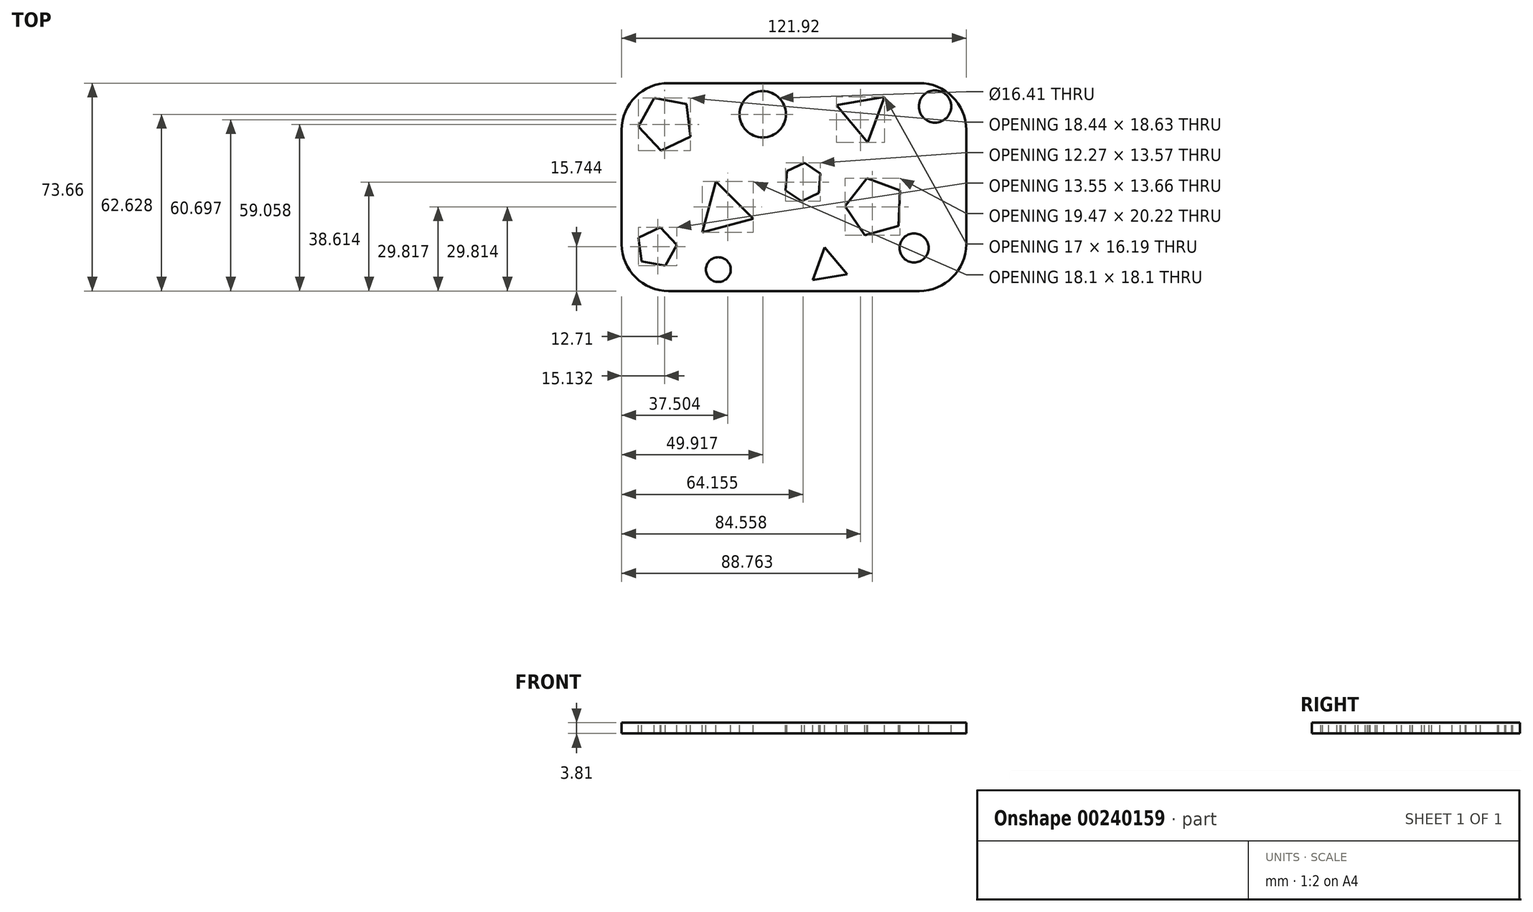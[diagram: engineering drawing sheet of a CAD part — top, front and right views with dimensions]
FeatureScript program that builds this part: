
annotation { "Feature Type Name" : "Feature", "Feature Type Description" : "" }
export const myFeature = defineFeature(function(context is Context, id is Id, definition is map)
    precondition{}
    {
        {
            var Q0;
            Q0=qCreatedBy(makeId("Top.planeOp"),FACE);
            var sketch = newSketch(context, id + "F0", { "sketchPlane" : qUnion([Q0])});
            skLineSegment(sketch, "E0.bottom", {"start": v(-58.63, 50.24) * mm, "end": v(63.29, 50.24) * mm});
            skLineSegment(sketch, "E0.top", {"start": v(-58.63, -23.42) * mm, "end": v(63.29, -23.42) * mm});
            skLineSegment(sketch, "E0.left", {"start": v(-58.63, 50.24) * mm, "end": v(-58.63, -23.42) * mm});
            skLineSegment(sketch, "E0.right", {"start": v(63.29, 50.24) * mm, "end": v(63.29, -23.42) * mm});
            skSolve(sketch);
        }
        {
            var Q0;
            Q0 = qSketchRegion(id + "F0", true);
            extrude(context, id + "F1", {"entities" : qUnion([Q0]), "depth" : 3.8 * mm});
        }
        {
            var Q0;
            Q0=makeQuery(id+"F1.opExtrude","SWEPT_EDGE",EDGE,{"disambiguationData":[OSD([sQuery(id+"F0.wireOp",EDGE,"E0.top"),sQuery(id+"F0.wireOp",EDGE,"E0.left")])]});
            var Q1;
            Q1=makeQuery(id+"F1.opExtrude","SWEPT_EDGE",EDGE,{"disambiguationData":[OSD([sQuery(id+"F0.wireOp",EDGE,"E0.top"),sQuery(id+"F0.wireOp",EDGE,"E0.right")])]});
            var Q2;
            Q2=makeQuery(id+"F1.opExtrude","SWEPT_EDGE",EDGE,{"disambiguationData":[OSD([sQuery(id+"F0.wireOp",EDGE,"E0.bottom"),sQuery(id+"F0.wireOp",EDGE,"E0.right")])]});
            var Q3;
            Q3=makeQuery(id+"F1.opExtrude","SWEPT_EDGE",EDGE,{"disambiguationData":[OSD([sQuery(id+"F0.wireOp",EDGE,"E0.bottom"),sQuery(id+"F0.wireOp",EDGE,"E0.left")])]});
            fillet(context, id + "F2", {"entities" : qUnion([Q0, Q1, Q2, Q3]), "radius" : 16.56 * mm, "tangentPropagation" : true, "allowEdgeOverflow" : false});
        }
        {
            var Q0;
            Q0=makeQuery(id+"F1.opExtrude","CAP_FACE",FACE,{"disambiguationData":[OSD([sQuery(id+"F0.wireOp",EDGE,"E0.bottom"),sQuery(id+"F0.wireOp",EDGE,"E0.top"),sQuery(id+"F0.wireOp",EDGE,"E0.left"),sQuery(id+"F0.wireOp",EDGE,"E0.right")])],"isStart":false});
            var sketch = newSketch(context, id + "F3", { "sketchPlane" : qUnion([Q0])});
            skCircle(sketch, "E1.cCircle", {"center": v(-42.93, 36.02) * mm, "radius": 7.99 * mm, "construction": true});
            skLineSegment(sketch, "E1.0", {"start": v(-34.28, 31.27) * mm, "end": v(-44.78, 26.32) * mm});
            skLineSegment(sketch, "E1.1", {"start": v(-44.78, 26.32) * mm, "end": v(-52.72, 34.78) * mm});
            skLineSegment(sketch, "E1.2", {"start": v(-52.72, 34.78) * mm, "end": v(-47.13, 44.95) * mm});
            skLineSegment(sketch, "E1.3", {"start": v(-47.13, 44.95) * mm, "end": v(-35.73, 42.78) * mm});
            skLineSegment(sketch, "E1.4", {"start": v(-35.73, 42.78) * mm, "end": v(-34.28, 31.27) * mm});
            skPoint(sketch, "E1.0.midPoint", {"position": v(-39.53, 28.8) * mm});
            skCircle(sketch, "E2.cCircle", {"center": v(31.03, 6.27) * mm, "radius": 8.6 * mm, "construction": true});
            skLineSegment(sketch, "E2.0", {"start": v(28.13, 16.5) * mm, "end": v(39.87, 12.18) * mm});
            skLineSegment(sketch, "E2.1", {"start": v(39.87, 12.18) * mm, "end": v(39.38, -0.31) * mm});
            skLineSegment(sketch, "E2.2", {"start": v(39.38, -0.31) * mm, "end": v(27.35, -3.71) * mm});
            skLineSegment(sketch, "E2.3", {"start": v(27.35, -3.71) * mm, "end": v(20.4, 6.68) * mm});
            skLineSegment(sketch, "E2.4", {"start": v(20.4, 6.68) * mm, "end": v(28.13, 16.5) * mm});
            skPoint(sketch, "E2.0.midPoint", {"position": v(34, 14.34) * mm});
            skCircle(sketch, "E3.cCircle", {"center": v(-46.33, -7.97) * mm, "radius": 5.86 * mm, "construction": true});
            skLineSegment(sketch, "E3.0", {"start": v(-45.01, -0.84) * mm, "end": v(-39.14, -7.02) * mm});
            skLineSegment(sketch, "E3.1", {"start": v(-39.14, -7.02) * mm, "end": v(-43.2, -14.5) * mm});
            skLineSegment(sketch, "E3.2", {"start": v(-43.2, -14.5) * mm, "end": v(-51.58, -12.96) * mm});
            skLineSegment(sketch, "E3.3", {"start": v(-51.58, -12.96) * mm, "end": v(-52.7, -4.51) * mm});
            skLineSegment(sketch, "E3.4", {"start": v(-52.7, -4.51) * mm, "end": v(-45.01, -0.84) * mm});
            skPoint(sketch, "E3.0.midPoint", {"position": v(-42.08, -3.93) * mm});
            skCircle(sketch, "E4", {"center": v(-8.71, 39.2) * mm, "radius": 8.2 * mm});
            skCircle(sketch, "E5", {"center": v(44.84, -8.18) * mm, "radius": 5.14 * mm});
            skCircle(sketch, "E6", {"center": v(-24.44, -15.83) * mm, "radius": 4.38 * mm});
            skCircle(sketch, "E7", {"center": v(52.28, 41.97) * mm, "radius": 5.72 * mm});
            skCircle(sketch, "E8.cCircle", {"center": v(-22.53, 5) * mm, "radius": 5.4 * mm, "construction": true});
            skLineSegment(sketch, "E8.0", {"start": v(-25.33, 15.44) * mm, "end": v(-12.08, 2.2) * mm});
            skLineSegment(sketch, "E8.1", {"start": v(-12.08, 2.2) * mm, "end": v(-30.18, -2.66) * mm});
            skLineSegment(sketch, "E8.2", {"start": v(-30.18, -2.66) * mm, "end": v(-25.33, 15.44) * mm});
            skPoint(sketch, "E8.0.midPoint", {"position": v(-18.7, 8.82) * mm});
            skCircle(sketch, "E9.cCircle", {"center": v(26.78, 39) * mm, "radius": 4.98 * mm, "construction": true});
            skLineSegment(sketch, "E9.0", {"start": v(28.47, 29.18) * mm, "end": v(17.43, 42.43) * mm});
            skLineSegment(sketch, "E9.1", {"start": v(17.43, 42.43) * mm, "end": v(34.43, 45.37) * mm});
            skLineSegment(sketch, "E9.2", {"start": v(34.43, 45.37) * mm, "end": v(28.47, 29.18) * mm});
            skPoint(sketch, "E9.0.midPoint", {"position": v(22.95, 35.8) * mm});
            skCircle(sketch, "E10.cCircle", {"center": v(14.45, -14.98) * mm, "radius": 3.56 * mm, "construction": true});
            skLineSegment(sketch, "E10.0", {"start": v(13.24, -7.96) * mm, "end": v(21.14, -17.44) * mm});
            skLineSegment(sketch, "E10.1", {"start": v(21.14, -17.44) * mm, "end": v(8.97, -19.55) * mm});
            skLineSegment(sketch, "E10.2", {"start": v(8.97, -19.55) * mm, "end": v(13.24, -7.96) * mm});
            skPoint(sketch, "E10.0.midPoint", {"position": v(17.19, -12.7) * mm});
            skCircle(sketch, "E11.cCircle", {"center": v(5.53, 15.2) * mm, "radius": 5.9 * mm, "construction": true});
            skLineSegment(sketch, "E11.0", {"start": v(-0.1, 19.03) * mm, "end": v(6.04, 21.98) * mm});
            skLineSegment(sketch, "E11.1", {"start": v(6.04, 21.98) * mm, "end": v(11.66, 18.14) * mm});
            skLineSegment(sketch, "E11.2", {"start": v(11.66, 18.14) * mm, "end": v(11.14, 11.35) * mm});
            skLineSegment(sketch, "E11.3", {"start": v(11.14, 11.35) * mm, "end": v(5, 8.4) * mm});
            skLineSegment(sketch, "E11.4", {"start": v(5, 8.4) * mm, "end": v(-0.6, 12.25) * mm});
            skLineSegment(sketch, "E11.5", {"start": v(-0.6, 12.25) * mm, "end": v(-0.1, 19.03) * mm});
            skPoint(sketch, "E11.0.midPoint", {"position": v(2.98, 20.5) * mm});
            skSolve(sketch);
        }
        {
            var Q0;
            Q0 = qSketchRegion(id + "F3", true);
            extrude(context, id + "F4", {"entities" : qUnion([Q0]), "operationType" : NewBodyOperationType.REMOVE, "endBound" : BoundingType.THROUGH_ALL, "oppositeDirection" : true, "depth" : 25.4 * mm});
        }
    });
